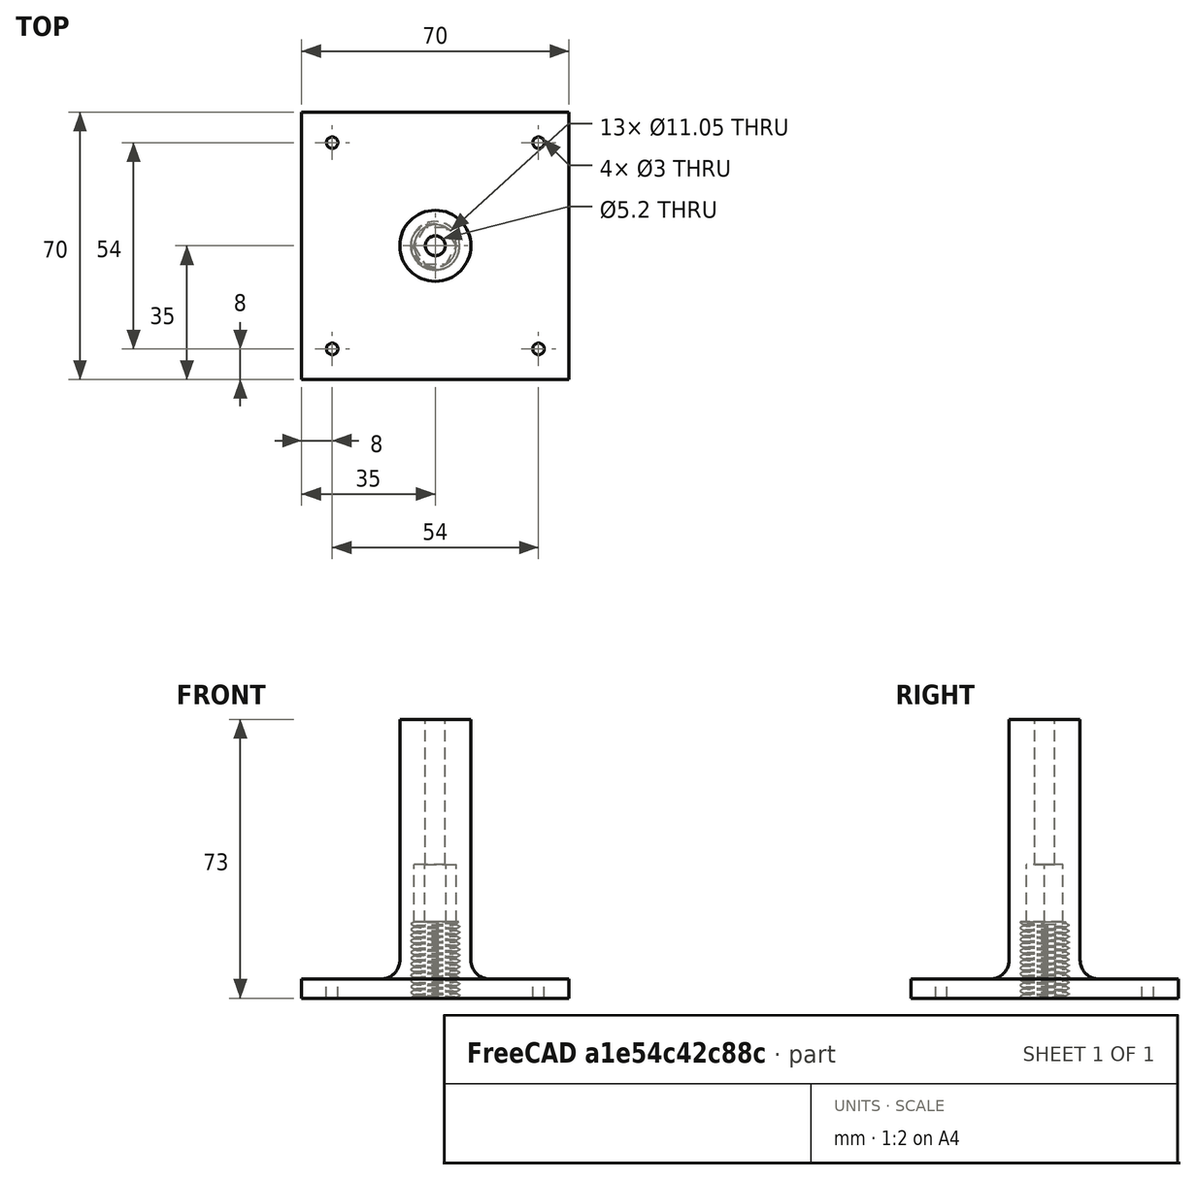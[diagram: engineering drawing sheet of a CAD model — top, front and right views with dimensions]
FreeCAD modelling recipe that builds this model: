
FCSTD DOCUMENT  (FreeCAD 0.17R13541 (Git))
Label: tip-changer-bottom
License: All rights reserved
LicenseURL: http://en.wikipedia.org/wiki/All_rights_reserved
objects: Part::Cylinder×11, Part::Cut×9, Spreadsheet::Sheet×2, Part::MultiFuse×2, Part::Box×1, Part::Prism×1, Part::Helix×1, Part::Fillet×1, PartDesign::FeatureBase×1, Sketcher::SketchObject×1, PartDesign::SubtractivePipe×1, PartDesign::Body×1, Mesh::Feature×1
note: 31 computed .brp shape members not serialized (recipe doc carries the construction recipe); baked Part::Feature solids carry a one-line shape summary decoded from their .brp

FEATURE [Spreadsheet::Sheet] Spreadsheet
  cells = A1=steigung; B1=h; D1(pitch)=1.5; F1=bauhöhe; G1(height)=20; A2=Gewindetiefe; B2=t; C2=h*cos(30°); D2(threaddepth)==pitch * cos(30); F2=helix height; G2(height_h)=25; C3=threaddepth tol; D3(threaddepth_tol)==(pitch + tolerance * cos(30)) * cos(30); F3=Flanken - Tolerance; G3(tolerance)=0; A4=Nut; F4=Radien - Tolerance; G4(tolerance_rad)=0.20000000000000001; A5=ra; E5(nut_ra)==bolt_ri + bolt_si + threaddepth + nut_sa; A6=sa; E6(nut_sa)=3; A7=ri; E7(nut_ri)==nb_centerline - threaddepth / 2 + threaddepth / 4 + tolerance_rad; A9=Bolt; A10=ri; E10(bolt_ri)==E16; A11=si; E11(bolt_si)==E17; G11==sqrt(1 / 6 ^ 2 - (tan(30) / 4) ^ 2) * Spreadsheet.threaddepth_tol; A12=ra; E12(bolt_ra)==nb_centerline + threaddepth / 2 - threaddepth / 8 - tolerance_rad; A14=Nut/Bold centerline; E14(nb_centerline)==bolt_ri + bolt_si + threaddepth / 2; A16=Spring rh; E16(spring_rh)==Tabelle1.B18 / 2 + Tabelle1.B3; A17=hülsenstärke sh; E17(spring_sh)==Tabelle1.B19; A18=join rest   js; E18(spring_sj)=1.3999999999999999; A21=join heigtht jh; B21(spring_jh)=3; A22=join ri; B22(spring_jri)==spring_rh + spring_sh + tolerance
FEATURE [Part::Cylinder] Cylinder012  label="Zylinder012"
  Angle = 360
  AttacherType = Attacher::AttachEngine3D
  Height = 20
  Radius = 9.29904
  expr: Height = Spreadsheet.height
  expr: Radius = Spreadsheet.nut_ra
FEATURE [Part::Cylinder] Cylinder  label="Zylinder"
  Angle = 360
  AttacherType = Attacher::AttachEngine3D
  Height = 53
  Placement = pos=(0,0,20) rot=(0,0,1;0rad)
  Radius = 9.29904
  expr: Placement.Base.z = Spreadsheet.G1
  expr: Height = Tabelle1.B33 - Spreadsheet.G1
  expr: Radius = Spreadsheet.E5
FEATURE [Part::Cylinder] Cylinder002  label="Zylinder002"
  Angle = 360
  AttacherType = Attacher::AttachEngine3D
  Height = 50
  Placement = pos=(0,0,34.3) rot=(0,0,1;0rad)
  Radius = 2.6
  expr: Radius = Tabelle1.B11 / 2 + Tabelle1.B3 / 2
FEATURE [Part::Cylinder] Cylinder024  label="Zylinder022"
  Angle = 360
  AttacherType = Attacher::AttachEngine3D
  Height = 10
  Placement = pos=(-27,27,0) rot=(0,0,1;0rad)
  Radius = 1.5
FEATURE [Part::Box] Box002  label="Quader001"
  AttacherType = Attacher::AttachEngine3D
  Height = 5
  Length = 70
  Placement = pos=(-35,-35,0) rot=(0,0,1;0rad)
  Width = 70
  expr: Placement.Base.x = -70 / 2
  expr: Placement.Base.y = -70 / 2
FEATURE [Part::Cylinder] Cylinder026  label="Zylinder024"
  Angle = 360
  AttacherType = Attacher::AttachEngine3D
  Height = 10
  Placement = pos=(27,27,0) rot=(0,0,1;0rad)
  Radius = 1.5
FEATURE [Part::Cylinder] Cylinder023  label="Zylinder021"
  Angle = 360
  AttacherType = Attacher::AttachEngine3D
  Height = 10
  Placement = pos=(-27,-27,0) rot=(0,0,1;0rad)
  Radius = 1.5
FEATURE [Part::Cylinder] Cylinder021  label="Zylinder019"
  Angle = 360
  AttacherType = Attacher::AttachEngine3D
  Height = 10
  Radius = 9.29904
  expr: Radius = Spreadsheet.E5
FEATURE [Part::Cylinder] Cylinder025  label="Zylinder023"
  Angle = 360
  AttacherType = Attacher::AttachEngine3D
  Height = 10
  Placement = pos=(27,-27,0) rot=(0,0,1;0rad)
  Radius = 1.5
FEATURE [Part::Prism] Prism001  label="Prisma001"
  AttacherType = Attacher::AttachEngine3D
  Circumradius = 5.52476
  Height = 15
  Placement = pos=(0,0,20) rot=(0,0,1;0rad)
  Polygon = 6
  expr: Circumradius = Spreadsheet.nut_ri
FEATURE [Part::Cut] Cut
  Base = -> Cylinder
  Tool = -> Prism001
FEATURE [Part::Cut] Cut061
  Base = -> Cut
  Tool = -> Cylinder002
FEATURE [Part::Cut] Cut033
  Base = -> Box002
  Tool = -> Cylinder021
FEATURE [Part::Helix] Helix004
  Angle = 0
  AttacherType = Attacher::AttachEngine3D
  Height = 25
  LocalCoord = 0
  Pitch = 1.5
  Radius = 5.52476
  Style = 1
  expr: Radius = Spreadsheet.nut_ri
  expr: Height = Spreadsheet.height_h
  expr: Pitch = Spreadsheet.pitch
FEATURE [Part::Cylinder] Cylinder034  label="Zylinder032"
  Angle = 360
  AttacherType = Attacher::AttachEngine3D
  Height = 20
  Radius = 9.29904
  expr: Radius = Spreadsheet.nut_ra
FEATURE [Part::Cylinder] Cylinder035  label="Zylinder033"
  Angle = 360
  AttacherType = Attacher::AttachEngine3D
  Height = 20
  Radius = 9.09904
  expr: Radius = Spreadsheet.nut_ra - 0.20000000000000001
FEATURE [Part::Cut] Cut056
  Base = -> Cylinder034
  Tool = -> Cylinder035
FEATURE [Part::MultiFuse] Fusion004
  Shapes = -> [Cut033,Cut056]
FEATURE [Part::Cut] Cut057
  Base = -> Fusion004
  Tool = -> Cylinder023
FEATURE [Part::Cut] Cut058
  Base = -> Cut057
  Tool = -> Cylinder024
FEATURE [Part::Cut] Cut059
  Base = -> Cut058
  Tool = -> Cylinder025
FEATURE [Part::Cut] Cut060
  Base = -> Cut059
  Tool = -> Cylinder026
FEATURE [Part::Fillet] Fillet
  Base = -> Cut060
  Edges = 1 edges r=5: [Edge12]
FEATURE [Spreadsheet::Sheet] Tabelle1
  cells = A1=Abstand Pip/Boden; B1=65; A3=Toleranz; B3=0.20000000000000001; A5=Teller; A6=Breite/Länge; B6=65; A7=Dicke; B7=5; A8=Befestigung höhe; B8=10; A10=Achse; A11=Durchmesser; B11=5; A12=Teller Befestigung; B12==B7 + B8; A13=Führung Länge; B13=40; C13=Wandstärke; D13=5; A14=Freiraum; B14=5; A15=Länge; B15==B14 + B13 + B12; A17=Feder; A18=Hülse durchmesser; B18=3.6000000000000001; A19=Hülse Wanddicke; B19=3; A20=L0; B20=25; A21=delta L; B21=3; A22=Spannmutter; A23=Höhe; B23=10; A24=Durchmesser Pitch; B24=20; A25=min Abstand Boden; B25=5; A28=min Oberkante Platte; B28==B25 + B23 + B20 + B19 + B13 + B7; A30=Gehäuse; A31=Wandstärke; B31=5; A32=Durchmesser; B32==B24 + 2 * B31; A33=Höhe; B33==B25 + B20 + B19 + B13; A35=Spitze d1; B35=7; A36=Spitze d2; B36=6.5; A37=Raster; B37=10.5; A38=Anzahl x/y; B38=6; A39=offset; B39==(Tabelle1.B6 - ((Tabelle1.B38 - 1) * Tabelle1.B37 + Tabelle1.B35)) / 2 + Tabelle1.B35 / 2
FEATURE [Part::Cylinder] Cylinder011  label="Zylinder011"
  Angle = 360
  AttacherType = Attacher::AttachEngine3D
  Height = 20
  Radius = 5.52476
  expr: Height = Spreadsheet.height
  expr: Radius = Spreadsheet.nut_ri
FEATURE [Part::Cut] Cut005
  Base = -> Cylinder012
  Tool = -> Cylinder011
FEATURE [PartDesign::FeatureBase] BaseFeature004
  BaseFeature = -> Cut005
FEATURE [Sketcher::SketchObject] CopySketch001
  Placement = pos=(0,0,0) rot=(1,0,0;1.5708rad)
  expr: Constraints[5] = Spreadsheet.pitch / 2
  expr: Constraints[20] = Spreadsheet.threaddepth_tol / 12
  expr: Constraints[17] = Spreadsheet.threaddepth_tol * (1 - 1 / 4 - 1 / 8)
  expr: Constraints[16] = Spreadsheet.threaddepth_tol * (1 - 1 / 4) * sin(30) / cos(30)
  expr: Constraints[1] = Spreadsheet.nut_ri - 0.001
  sketch-geometry (7):
    g0: LineSegment [constr] StartX=0 StartY=0 StartZ=0 EndX=5.52376 EndY=0 EndZ=0
    g1: LineSegment [constr] StartX=5.52376 StartY=0 StartZ=0 EndX=5.52376 EndY=-0.75 EndZ=0
    g2: LineSegment StartX=5.52376 StartY=-0.75 StartZ=0 EndX=5.52376 EndY=-0.1875 EndZ=0
    g3: LineSegment StartX=5.52376 StartY=-0.75 StartZ=0 EndX=5.52376 EndY=-1.3125 EndZ=0
    g4: LineSegment StartX=5.52376 StartY=-1.3125 StartZ=0 EndX=6.33566 EndY=-0.84375 EndZ=0
    g5: LineSegment StartX=5.52376 StartY=-0.1875 StartZ=0 EndX=6.33566 EndY=-0.65625 EndZ=0
    g6: ArcOfCircle CenterX=6.28153 CenterY=-0.75 CenterZ=0 NormalX=0 NormalY=0 NormalZ=1 AngleXU=0 Radius=0.108253 StartAngle=5.23599 EndAngle=7.33038
  constraints (21):
    c: Horizontal(g0)
    c: DistanceX(g0,g0) = 5.52376
    c: Coincident(g-1,g0)
    c: Coincident(g1,g0)
    c: Vertical(g1)
    c: DistanceY(g1,g1) = 0.75
    c: Vertical(g2)
    c: Coincident(g3,g2)
    c: Vertical(g3)
    c: Equal(g2,g3)
    c: Coincident(g4,g3)
    c: Coincident(g5,g2)
    c: Coincident(g2,g1)
    c: Equal(g5,g4)
    c: Angle(g2,g5) = 1.0472
    c: Angle(g4,g3) = 1.0472
    c: DistanceY(g3,g3) = 0.5625
    c: DistanceX(g5,g5) = 0.811899
    c: Coincident(g6,g5)
    c: Coincident(g6,g4)
    c: Radius(g6) = 0.108253
FEATURE [PartDesign::SubtractivePipe] SubtractivePipe004
  AuxilleryCurvelinear = true
  AuxillerySpineTangent = false
  BaseFeature = -> BaseFeature004
  Binormal = (0,0,0)
  Mode = 2
  Profile = -> CopySketch001
  Spine = -> Helix004 [Edge1,Edge2,Edge3,Edge4,Edge5,Edge6,Edge7,Edge8,Edge9,Edge10,Edge11,Edge12,Edge13,Edge14]
  SpineTangent = false
  Transformation = 0
  Transition = 0
FEATURE [PartDesign::Body] Body007  label="JoinNut"
  BaseFeature = -> Cut005
  Group = -> [BaseFeature004,SubtractivePipe004]
  Origin = -> Origin010
  Tip = -> SubtractivePipe004
FEATURE [Part::MultiFuse] Fusion007  label="tip-changer-bottom"
  Shapes = -> [Body007,Cut061,Fillet]
FEATURE [Mesh::Feature] Mesh  label="tip-changer-bottom (Meshed)"
